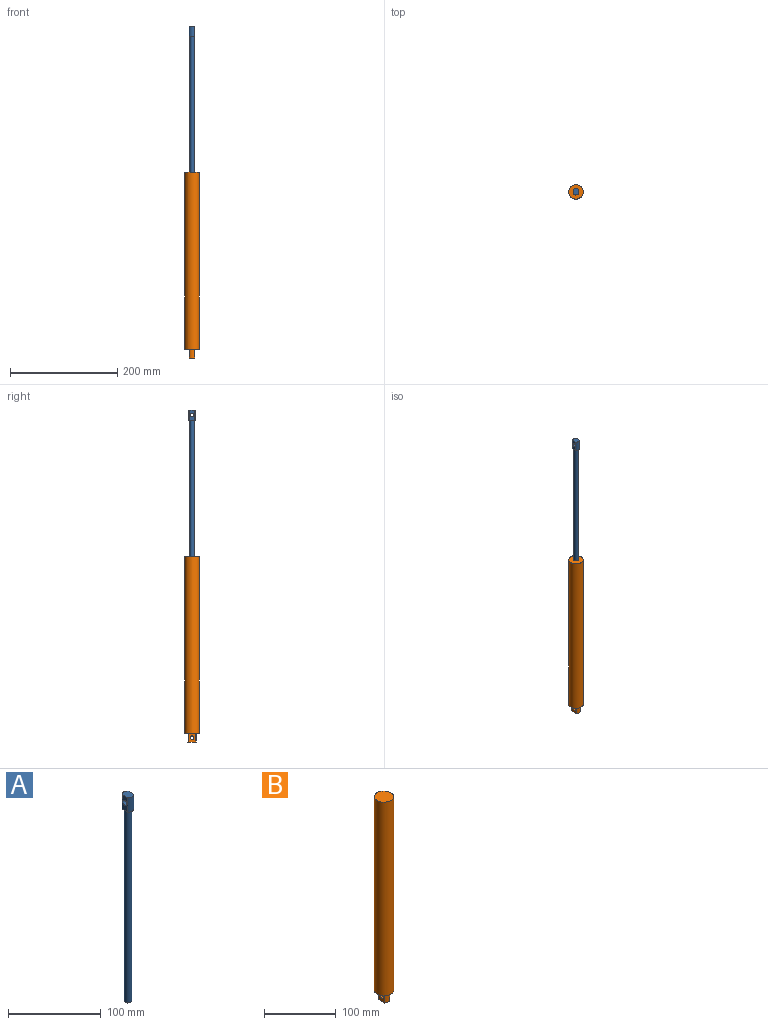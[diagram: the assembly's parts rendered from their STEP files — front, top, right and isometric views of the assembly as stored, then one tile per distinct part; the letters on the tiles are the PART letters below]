
ASSEMBLY  parts=2 mates=1
PART A: 9 faces, bbox 9.5x12.7x273.1 mm
  f0: plane 19.05x8.4mm, normal (-1,0,0), area 128.4mm2, adj f1,f3,f4,f5,f6
  f1: cylinder r=6.35mm len=19.05mm, axis (0,0,-1), area 205.2mm2, adj f0,f2,f4,f5
  f2: plane 19.05x8.4mm, normal (1,0,0), area 128.4mm2, adj f1,f3,f4,f5,f6
  f3: cylinder r=6.35mm len=19.05mm, axis (0,0,-1), area 205.2mm2, adj f0,f2,f4,f5
  f4: plane 12.7x9.53mm, normal (0,0,1), area 108.4mm2, adj f0,f1,f2,f3
  f5: plane 12.7x9.53mm, normal (0,0,-1), area 58.9mm2, adj f0,f1,f2,f3,f7
  f6: cylinder r=3.17mm len=9.53mm, axis (-1,0,0), area 190mm2, adj f0,f2
  f7: cylinder r=3.97mm len=254mm, axis (0,0,1), area 6333.8mm2, adj f5,f8
  f8: plane 7.94x7.94mm, normal (0,0,-1), area 49.5mm2, adj f7
PART B: 9 faces, bbox 27x27x346.5 mm
  f0: plane 26.99x26.99mm, normal (0,0,-1), area 430.5mm2, adj f1,f3,f4,f5,f6
  f1: cylinder r=13.49mm len=330.2mm, axis (0,0,-1), area 27995.6mm2, adj f0,f2
  f2: plane 26.99x26.99mm, normal (0,0,1), area 572mm2, adj f1
  f3: plane 16.26x12.7mm, normal (1,0,0), area 174.8mm2, adj f0,f4,f6,f7,f8
  f4: cylinder r=7.94mm len=16.26mm, axis (0,0,1), area 166.1mm2, adj f0,f3,f5,f7
  f5: plane 16.26x12.7mm, normal (-1,0,0), area 174.8mm2, adj f0,f4,f6,f7,f8
  f6: cylinder r=7.94mm len=16.26mm, axis (0,0,1), area 166.1mm2, adj f0,f3,f5,f7
  f7: plane 15.88x9.53mm, normal (0,0,-1), area 141.6mm2, adj f3,f4,f5,f6
  f8: cylinder r=3.17mm len=9.53mm, axis (1,0,0), area 190mm2, adj f3,f5
PLACE A t=(0,0,254)mm
PLACE B at identity fixed
MATE slider B.f1 <-> A.f1  axis (0,0,1) through (0,0,330.2)mm
